# Revit family: CIRD
name_source: partatom
category: Lighting Fixtures
units: mm (PartAtom-declared; Revit-internal decimal feet)

## family parameters
Cut with Voids When Loaded = No
Host = Face
Light Source = No
OmniClass Number = 23.80.70.11.11
OmniClass Title = General Luminaries, Non Directional
Part Type = Normal
Room Calculation Point = No
Round Connector Dimension = Use Diameter
Shared = No

## types (1)
- CIRD
    Apparent Load = 1 VA
    Application = Stair-wells,Hallways,Offices and other commercial applications
    Body = Paint - Matte White
    Certification = UL924
    Default Elevation = 48 "
    Description = The Round Wall Forms luminaires include five configurations to suit any building application. The classic spherical shape and cross bar design have become an icon in outdoor lighting. An ADA compliant cutoff downlight design provides perimeter lighting while enhancing architecture.
    Features = Single or Double, white or black lamp-head
remote with base-plate
• LED life-cycle of more than 10 years
• Quick installation
• Damp Location Listed
• Fully adjustable lamp-heads
    Glass = Glass - White
    Lamp = LED
    Manufacturer = Compass Products
    Model = CIRD
    Steel = Metal-Galvanized_Steel
    Type Comments = Light Fixture
    URL = https://www.currentlighting.com
    Warranty = 2 year full unit warranty
    Wattage Comments = 1W

## geometry (parser evidence)
native form markers: Sweep x5
no freeform markers — native parametric forms only
